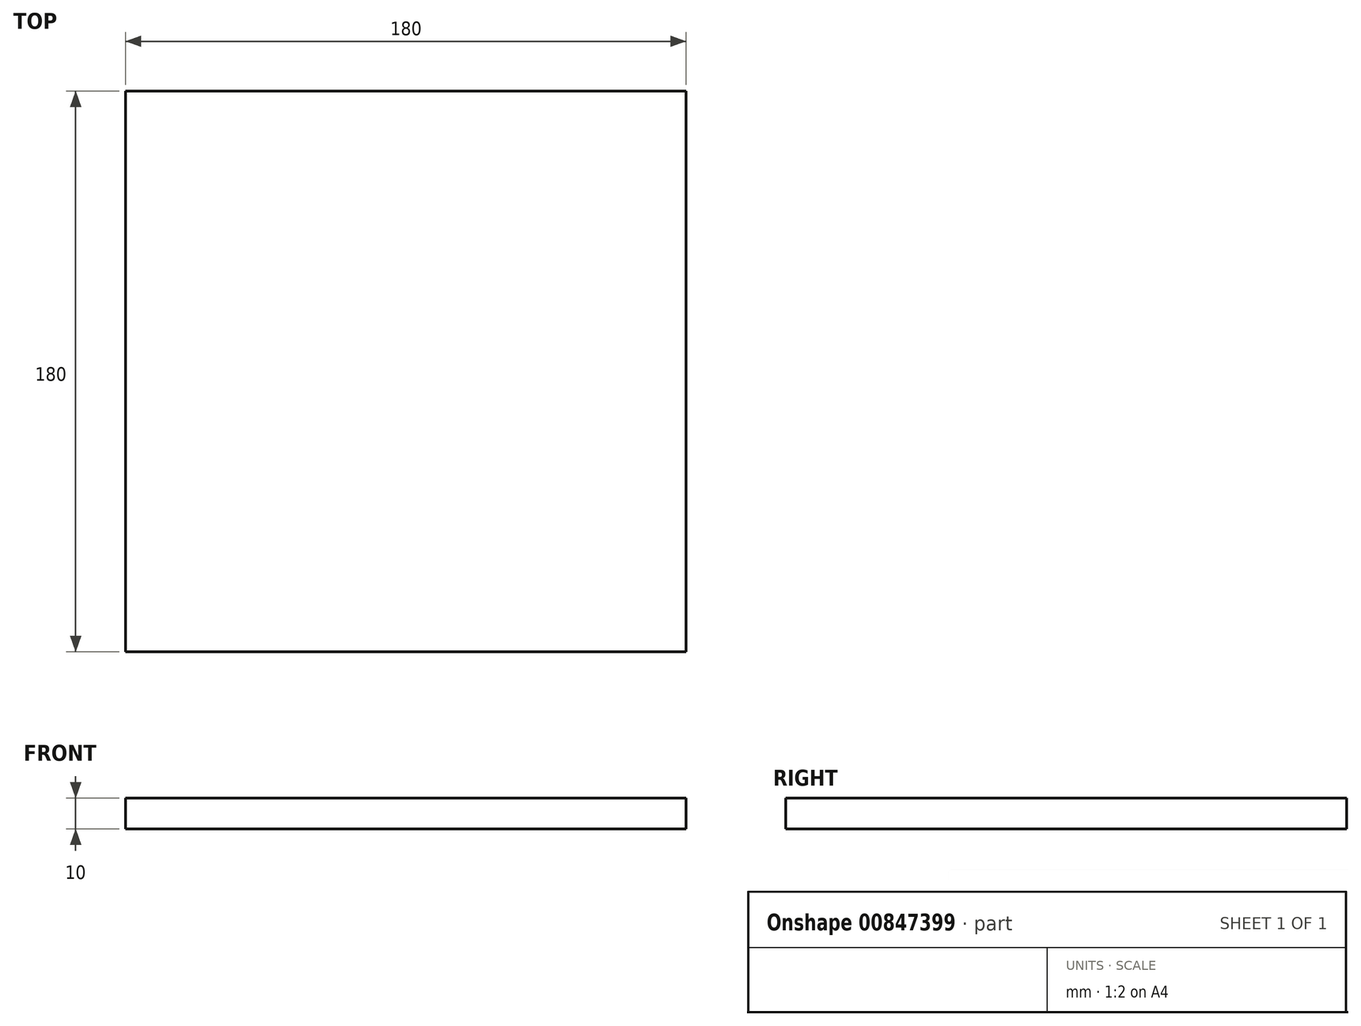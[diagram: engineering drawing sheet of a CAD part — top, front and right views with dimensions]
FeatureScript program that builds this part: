
annotation { "Feature Type Name" : "Feature", "Feature Type Description" : "" }
export const myFeature = defineFeature(function(context is Context, id is Id, definition is map)
    precondition{}
    {
        {
            var Q0;
            Q0=qCreatedBy(makeId("Top.planeOp"),FACE);
            var sketch = newSketch(context, id + "F0", { "sketchPlane" : qUnion([Q0])});
            skLineSegment(sketch, "E0.bottom", {"start": v(-195, 147.77) * mm, "end": v(-15, 147.77) * mm});
            skLineSegment(sketch, "E0.top", {"start": v(-195, -32.23) * mm, "end": v(-15, -32.23) * mm});
            skLineSegment(sketch, "E0.left", {"start": v(-195, 147.77) * mm, "end": v(-195, -32.23) * mm});
            skLineSegment(sketch, "E0.right", {"start": v(-15, 147.77) * mm, "end": v(-15, -32.23) * mm});
            skSolve(sketch);
        }
        {
            var Q0;
            Q0=makeQuery(id+"F0.imprint","IMPRINT",FACE,{"disambiguationData":[TD([[makeQuery(id+"F0.imprint","IMPRINT",EDGE,{"derivedFrom":sQuery(id+"F0.wireOp",EDGE,"E0.bottom")}),-1.0]])]});
            extrude(context, id + "F1", {"entities" : qUnion([Q0]), "depth" : 10 * mm, "offsetDistance" : 25 * mm});
        }
    });
